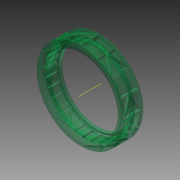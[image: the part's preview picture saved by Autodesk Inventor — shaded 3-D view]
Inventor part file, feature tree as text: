
AUTODESK INVENTOR PART (.ipt)
format: ipt  version: 2013 (Build 170138000, 138)  size: 2,126,336 bytes
history: native  units: in
note: dims shown in document units (in); Inventor stores cm internally (conversion verified against a paired STEP export)
features: sketch x11, plane x6, extrude x4, pattern_circular x3, sweep x3, revolve x1, other x1, mirror x1, fillet x1
ambient origin geometry x8: Origin, YZ Plane, XZ Plane, XY Plane, X Axis, Y Axis, Z Axis, Center Point
bodies: Solid1 (feature_tree)
feature tree (31):
  revolve  "Revolution1"  [1 undecoded]
  extrude  "Extrusion1"  Depth=0.04in
  pattern_circular  "Circular Pattern1"  [2 undecoded]
  plane  "Work Plane1"
  other  "Work Axis1"
  extrude  "Extrusion2"  Depth=0.016in
  pattern_circular  "Circular Pattern3"  [2 undecoded]
  plane  "Work Plane3"
  plane  "Work Plane5"
  extrude  "Extrusion3"  Depth=0.03in
  extrude  "Extrusion4"  Depth=0.039in
  plane  "Work Plane6"
  sweep  "Sweep1"
  plane  "Work Plane7"
  sweep  "Sweep2"
  mirror  "Mirror1"
  sketch  "Sketch11"  dims[d13=0.012in]
  plane  "Work Plane8"
  sweep  "Sweep3"
  pattern_circular  "Circular Pattern4"  [2 undecoded]
  fillet  "Fillet1"  Radius=0.038in
  sketch  "Sketch2"  dims[d2=0.439in d3=0.347in]
  sketch  "Sketch3"  dims[d4=0.006in d5=0.04in]
  sketch  "Sketch6"  dims[d7=0.079in]
  sketch  "Sketch7"  dims[d8=0.012in]
  sketch  "Sketch8"  dims[d9=0.16in]
  sketch  "Sketch9"  dims[d11=0.039in]
  sketch  "3D Sketch1"
  sketch  "Sketch10"  dims[d12=0.008in]
  sketch  "3D Sketch2"
  sketch  "Sketch12"  dims[d14=0.012in d15=0.063in d16=0.016in d17=0.016in d18=0.03in d19=0.039in d20=0.013in d21=0.012in d22=0.165in d24=0.073in d25=0.038in d26=1.618in d28=0.237in d29=0.205in d30=0.042in d31=90.0deg d32=3.66in d33=3.5in d35=0.0962in d36=11.811in d38=360.0deg d40=0.147in d41=1.83in d42=1.75in d43=0.7in d44=0.0in d45=11.811in d46=360.0deg d67=0.05in d68=0.1718in d69=0.1718in d70=0.82in d71=0.0in d72=6.2992in d73=360.0deg d79=0.15in d80=0.015in d81=0.025in d82=0.025in d83=0.025in d84=0.025in d85=0.025in d86=0.025in d88=0.82in d89=0.0in d90=4.5in d91=0.0in d92=0.0in d93=0.1718in d94=0.1718in d96=0.0in d97=0.1718in d98=0.0in d99=0.1718in d100=0.1718in d101=0.05in d102=0.01in d103=0.0in d104=3.1496in d105=360.0deg d107=0.012in]
note: 7 required parameter values undecoded (feature->parameter linkage not recoverable at this tier; creation-order binding heuristic only, values carry confidence <= 0.55)